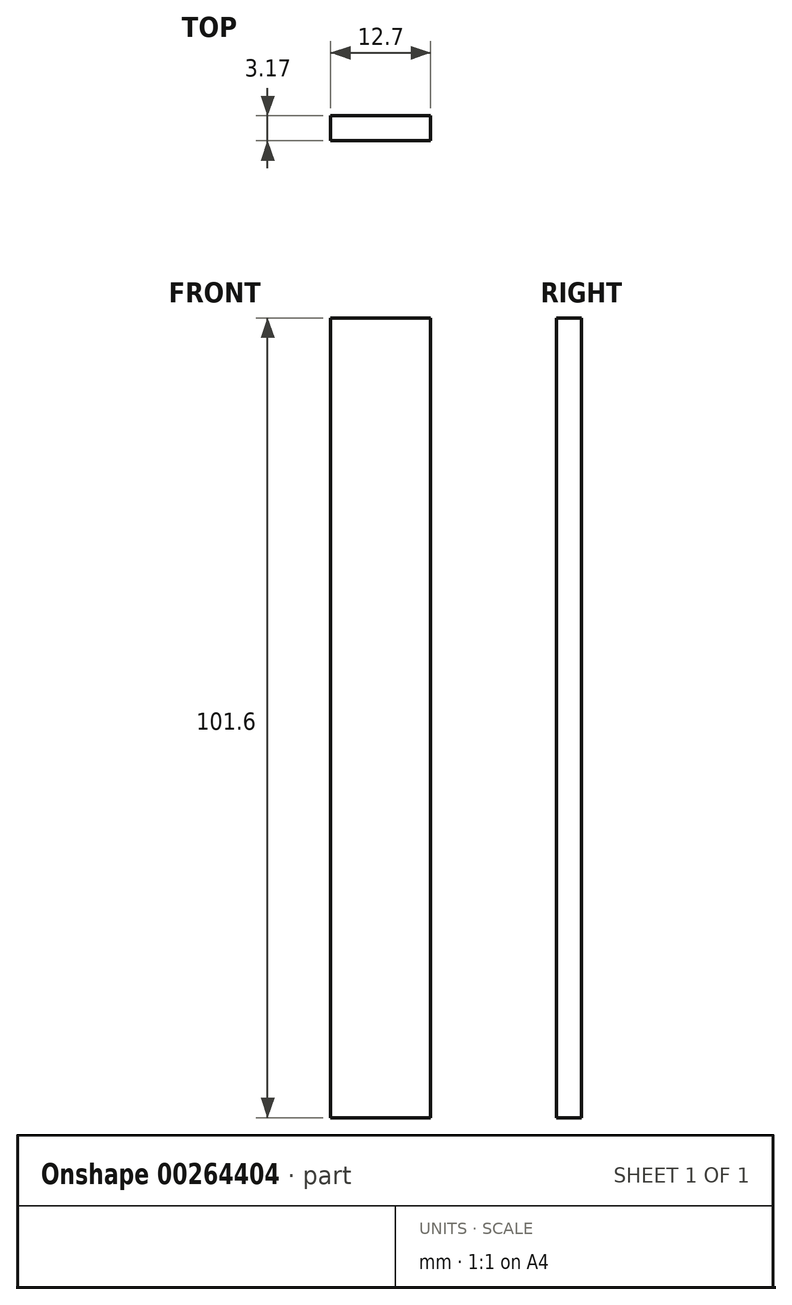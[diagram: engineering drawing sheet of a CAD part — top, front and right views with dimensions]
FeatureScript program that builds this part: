
annotation { "Feature Type Name" : "Feature", "Feature Type Description" : "" }
export const myFeature = defineFeature(function(context is Context, id is Id, definition is map)
    precondition{}
    {
        {
            var Q0;
            Q0=qCreatedBy(makeId("Front.planeOp"),FACE);
            var sketch = newSketch(context, id + "F0", { "sketchPlane" : qUnion([Q0])});
            skLineSegment(sketch, "E0.bottom", {"start": v(0, 0) * mm, "end": v(-12.7, 0) * mm});
            skLineSegment(sketch, "E0.top", {"start": v(0, 101.6) * mm, "end": v(-12.7, 101.6) * mm});
            skLineSegment(sketch, "E0.left", {"start": v(0, 0) * mm, "end": v(0, 101.6) * mm});
            skLineSegment(sketch, "E0.right", {"start": v(-12.7, 0) * mm, "end": v(-12.7, 101.6) * mm});
            skSolve(sketch);
        }
        {
            var Q0;
            Q0=makeQuery(id+"F0.imprint","IMPRINT",FACE,{"disambiguationData":[TD([[makeQuery(id+"F0.imprint","IMPRINT",EDGE,{"derivedFrom":sQuery(id+"F0.wireOp",EDGE,"E0.bottom")}),-1.0]])]});
            extrude(context, id + "F1", {"entities" : qUnion([Q0]), "depth" : 3.17 * mm});
        }
    });
